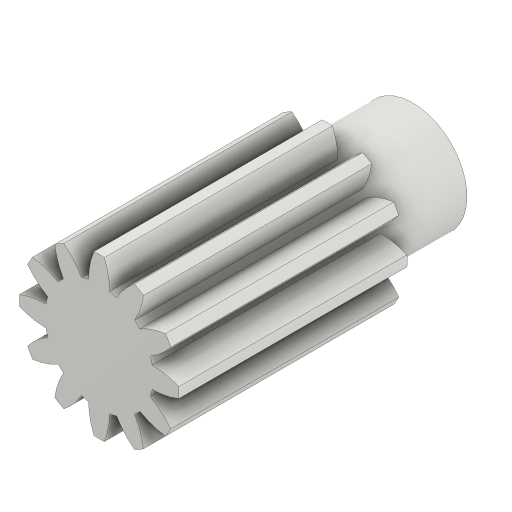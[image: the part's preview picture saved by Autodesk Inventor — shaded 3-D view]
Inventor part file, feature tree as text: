
AUTODESK INVENTOR PART (.ipt)
format: ipt  version: 2024 (Build 280153000, 153)  size: 374,784 bytes
history: native  units: mm (DEFAULTED — no unit token found)
features: extrude x4, sketch x4, plane x3, other x3, projected_geometry x1
ambient origin geometry x8: Origin, YZ Plane, XZ Plane, XY Plane, X Axis, Y Axis, Z Axis, Center Point
bodies: Solid1 (feature_tree)
feature tree (15):
  extrude  "Extrusion1"  Depth=20.0mm TaperAngle=0.0deg
  plane  "Work Plane2"
  plane  "Work Plane8"
  plane  "Work Plane9"
  other  "Spur Gear"
  extrude  "Extrusion2"  Depth=10.0mm TaperAngle=0.0deg
  extrude  "Extrusion3"  TaperAngle=0.0deg  [1 undecoded]
  extrude  "Extrusion4"  TaperAngle=0.0deg  [1 undecoded]
  sketch  "Sketch1"  dims[d0=28.0mm d1=20.0mm d2=0.0mm]
  other  "Srf1"
  sketch  "Sketch3"  dims[d3=24.0mm d4=10.0mm d5=0.0mm]
  projected_geometry  "Projected Loop1"
  sketch  "Sketch4"  dims[d16=60.0mm d17=0.0mm d34=15.0deg]
  sketch  "Sketch5"  dims[d39=0.0mm d41=0.0mm d43=60.0mm d46=60.0mm d47=0.0mm d48=0.0mm d49=20.0mm d50=0.0mm d51=15.0mm d52=0.0mm d53=7.0mm d54=180.0deg d55=3.0mm d56=15.0mm d57=0.0mm]
  other  "Pitch Diameter"
note: 2 required parameter values undecoded (feature->parameter linkage not recoverable at this tier; creation-order binding heuristic only, values carry confidence <= 0.55)
